# Revit family: Sink-Under_Mount-Kitchen-KOHLER-Vault-K-25939_1
name_source: partatom
category: Plumbing Fixtures
revit_build: Autodesk Revit 2017 (Build: 20160225_1515(x64)
units: mm (PartAtom-declared; Revit-internal decimal feet)

## family parameters
Cut with Voids When Loaded = No
Host = Face
OmniClass Number = 23.31.13.00
OmniClass Title = Sinks
Part Type = Normal
Room Calculation Point = No
Round Connector Dimension = Use Diameter
Shared = No

## types (1)
- NA-Stainless
    ADA Compliant = Yes
    Assembly Code = D2010400
    CW Connection = No
    Cold Water Inlet = Cold Water Inlet
    Date Modified = 08/20/2020
    Default Elevation = 36"
    Description = 32inch x 18-5/16inch x 5-7/9inch Undermount large single-bowl kitchen sink with no faucet holes
    Drain Included = No
    Finish = Kohler-Metal-NA-Stainless
    HW Connection = No
    Height = 5 13/16"
    Hot Water Inlet = Hot Water Inlet
    Length = 32"
    Manufacturer = KOHLER Co.
    Master Format 2014 = 22 41 16
    Master Format 2014 Name = Residential Lavatories and Sinks
    Material = Premium 18-Gauge Stainless Steel.
    Model = K-25939-NA
    Product Documentation Link = https://www.us.kohler.com
    Product Name = Vault
    Product Page URL = http://www.us.kohler.com
    Type = 1
    URL = https://www.us.kohler.com
    Vent Connection = No
    Waste Connection = Yes
    Waste Water Outlet = Waste Water Outlet
    WaterSense Certified = No
    Width = 18 5/16"

## geometry (parser evidence)
native form markers: Sweep x4
no freeform markers — native parametric forms only
